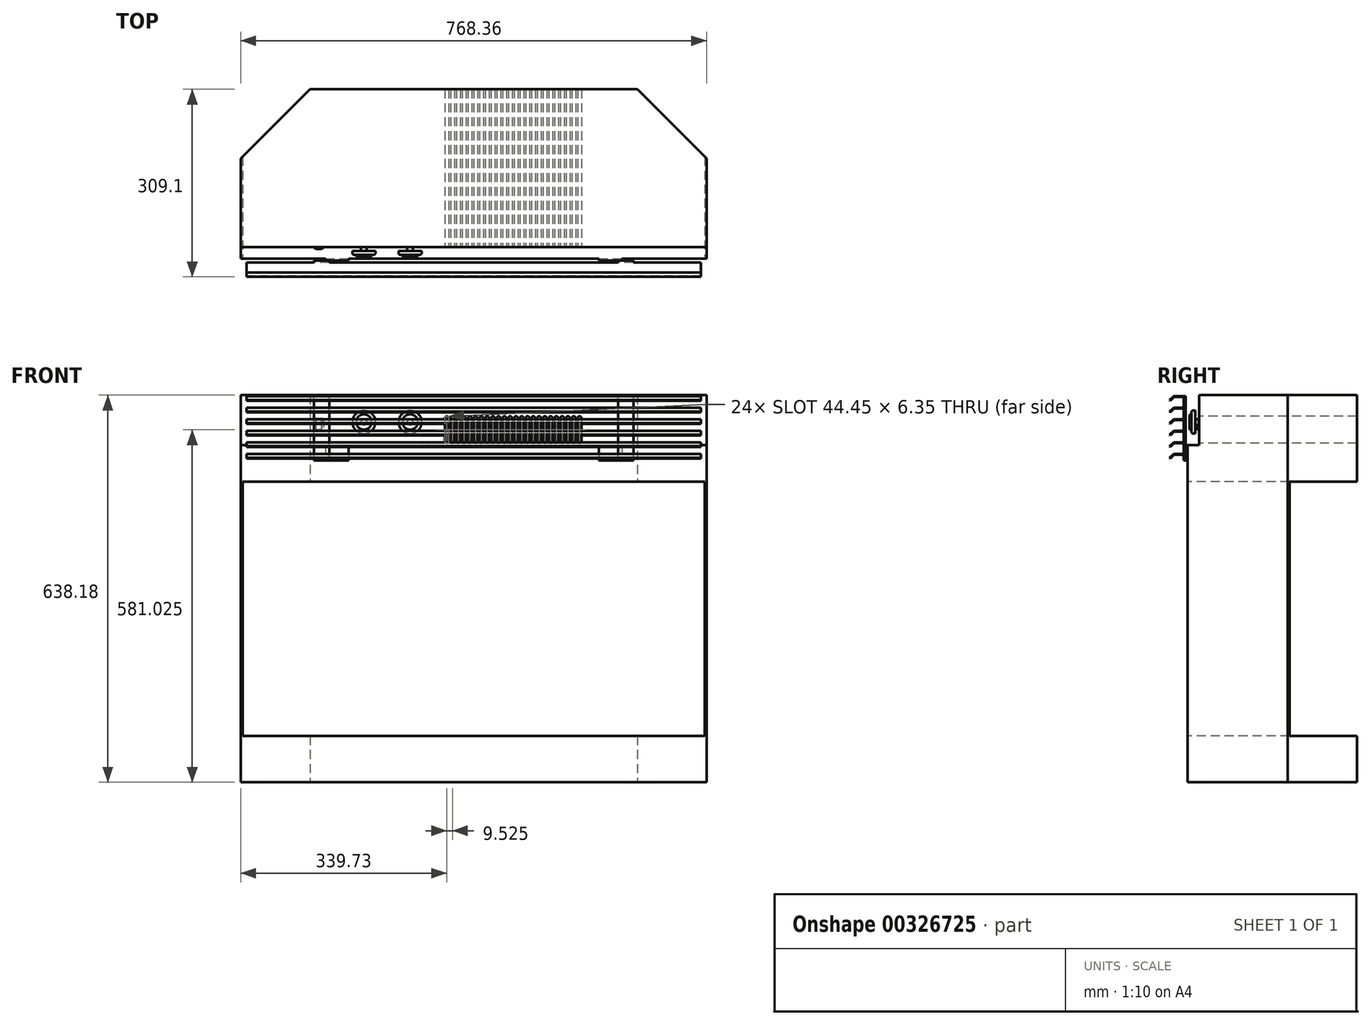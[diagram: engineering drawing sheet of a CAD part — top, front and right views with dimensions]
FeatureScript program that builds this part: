
annotation { "Feature Type Name" : "Feature", "Feature Type Description" : "" }
export const myFeature = defineFeature(function(context is Context, id is Id, definition is map)
    precondition{}
    {
        {
            var Q0;
            Q0=qCreatedBy(makeId("Top.planeOp"),FACE);
            var sketch = newSketch(context, id + "F0", { "sketchPlane" : qUnion([Q0])});
            skLineSegment(sketch, "E0.bottom", {"start": v(-269.88, 260.35) * mm, "end": v(269.88, 260.35) * mm});
            skLineSegment(sketch, "E0.top", {"start": v(-384.18, 0) * mm, "end": v(384.18, 0) * mm});
            skLineSegment(sketch, "E0.left", {"start": v(-384.18, 146.05) * mm, "end": v(-384.18, 0) * mm});
            skLineSegment(sketch, "E0.right", {"start": v(384.18, 146.05) * mm, "end": v(384.18, 0) * mm});
            skLineSegment(sketch, "E1", {"start": v(-384.18, 146.05) * mm, "end": v(-269.88, 260.35) * mm});
            skLineSegment(sketch, "E2", {"start": v(269.88, 260.35) * mm, "end": v(384.18, 146.05) * mm});
            skSolve(sketch);
        }
        {
            var Q0;
            Q0=makeQuery(id+"F0.imprint","IMPRINT",FACE,{"disambiguationData":[TD([[makeQuery(id+"F0.imprint","IMPRINT",EDGE,{"derivedFrom":sQuery(id+"F0.wireOp",EDGE,"E0.bottom")}),-1.0]])]});
            extrude(context, id + "F1", {"entities" : qUnion([Q0]), "depth" : 638.17 * mm});
        }
        {
            var Q0;
            Q0=makeQuery(id+"F1.opExtrude","SWEPT_FACE",FACE,{"disambiguationData":[OSD([sQuery(id+"F0.wireOp",EDGE,"E0.top")])]});
            var sketch = newSketch(context, id + "F2", { "sketchPlane" : qUnion([Q0])});
            skLineSegment(sketch, "E3.bottom", {"start": v(-384.18, 0) * mm, "end": v(384.18, 0) * mm});
            skLineSegment(sketch, "E3.top", {"start": v(-384.18, 555.62) * mm, "end": v(384.18, 555.62) * mm});
            skLineSegment(sketch, "E3.left", {"start": v(-384.18, 0) * mm, "end": v(-384.18, 555.62) * mm});
            skLineSegment(sketch, "E3.right", {"start": v(384.18, 0) * mm, "end": v(384.18, 555.62) * mm});
            skSolve(sketch);
        }
        {
            var Q0;
            Q0 = qSketchRegion(id + "F2", true);
            extrude(context, id + "F3", {"entities" : qUnion([Q0]), "operationType" : NewBodyOperationType.ADD, "depth" : 19.05 * mm});
        }
        {
            var Q0;
            Q0=makeQuery(id+"F3.opExtrude","CAP_FACE",FACE,{"disambiguationData":[OSD([sQuery(id+"F2.wireOp",EDGE,"E3.bottom"),sQuery(id+"F2.wireOp",EDGE,"E3.top"),sQuery(id+"F2.wireOp",EDGE,"E3.left"),sQuery(id+"F2.wireOp",EDGE,"E3.right")])],"isStart":false});
            var sketch = newSketch(context, id + "F4", { "sketchPlane" : qUnion([Q0])});
            skLineSegment(sketch, "E4.bottom", {"start": v(-381, 76.2) * mm, "end": v(381, 76.2) * mm});
            skLineSegment(sketch, "E4.top", {"start": v(-381, 495.3) * mm, "end": v(381, 495.3) * mm});
            skLineSegment(sketch, "E4.left", {"start": v(-381, 76.2) * mm, "end": v(-381, 495.3) * mm});
            skLineSegment(sketch, "E4.right", {"start": v(381, 76.2) * mm, "end": v(381, 495.3) * mm});
            skSolve(sketch);
        }
        {
            var Q0;
            Q0 = qSketchRegion(id + "F4", true);
            extrude(context, id + "F5", {"entities" : qUnion([Q0]), "operationType" : NewBodyOperationType.REMOVE, "endBound" : BoundingType.UP_TO_NEXT, "oppositeDirection" : true, "depth" : 6.35 * mm});
        }
        {
            var Q0;
            Q0=makeQuery(id+"F1.opExtrude","SWEPT_FACE",FACE,{"disambiguationData":[OSD([sQuery(id+"F0.wireOp",EDGE,"E0.top")])]});
            var sketch = newSketch(context, id + "F6", { "sketchPlane" : qUnion([Q0])});
            skCircle(sketch, "E5", {"center": v(-180.98, 593.73) * mm, "radius": 4.76 * mm});
            skCircle(sketch, "E6", {"center": v(-104.78, 593.73) * mm, "radius": 4.76 * mm});
            skSolve(sketch);
        }
        {
            var Q0;
            Q0=makeQuery(id+"F6.imprint","IMPRINT",FACE,{"disambiguationData":[TD([[makeQuery(id+"F6.imprint","IMPRINT",EDGE,{"derivedFrom":sQuery(id+"F6.wireOp",EDGE,"E5")}),1.0]])]});
            var Q1;
            Q1=makeQuery(id+"F6.imprint","IMPRINT",FACE,{"disambiguationData":[TD([[makeQuery(id+"F6.imprint","IMPRINT",EDGE,{"derivedFrom":sQuery(id+"F6.wireOp",EDGE,"E6")}),1.0]])]});
            extrude(context, id + "F7", {"entities" : qUnion([Q0, Q1]), "operationType" : NewBodyOperationType.ADD, "depth" : 6.35 * mm});
        }
        {
            var Q0;
            Q0=makeQuery(id+"F7.opExtrude","CAP_FACE",FACE,{"disambiguationData":[OSD([sQuery(id+"F6.wireOp",EDGE,"E5")])],"isStart":false});
            var sketch = newSketch(context, id + "F8", { "sketchPlane" : qUnion([Q0])});
            skCircle(sketch, "E7", {"center": v(-180.98, 593.73) * mm, "radius": 19.05 * mm});
            skCircle(sketch, "E8", {"center": v(-104.78, 593.73) * mm, "radius": 19.05 * mm});
            skSolve(sketch);
        }
        {
            var Q0;
            Q0=makeQuery(id+"F8.imprint","IMPRINT",FACE,{"disambiguationData":[TD([[makeQuery(id+"F8.imprint","IMPRINT",EDGE,{"derivedFrom":sQuery(id+"F8.wireOp",EDGE,"E8")}),1.0]])]});
            var Q1;
            Q1=makeQuery(id+"F8.imprint","IMPRINT",FACE,{"disambiguationData":[TD([[makeQuery(id+"F8.imprint","IMPRINT",EDGE,{"derivedFrom":sQuery(id+"F8.wireOp",EDGE,"E7")}),1.0]])]});
            var Q2;
            Q2=makeQuery(id+"F8.imprint","IMPRINT",FACE,{"disambiguationData":[TD([[makeQuery(id+"F8.imprint","IMPRINT",EDGE,{"derivedFrom":makeQuery(id+"F7.opExtrude","CAP_EDGE",EDGE,{"disambiguationData":[OSD([sQuery(id+"F6.wireOp",EDGE,"E5")])],"isStart":false})}),1.0]])]});
            extrude(context, id + "F9", {"entities" : qUnion([Q0, Q1, Q2]), "operationType" : NewBodyOperationType.ADD, "depth" : 6.35 * mm});
        }
        {
            var Q0;
            Q0=makeQuery(id+"F9.opExtrude","CAP_EDGE",EDGE,{"disambiguationData":[OSD([sQuery(id+"F8.wireOp",EDGE,"E8")])],"isStart":false});
            var Q1;
            Q1=makeQuery(id+"F9.opExtrude","CAP_EDGE",EDGE,{"disambiguationData":[OSD([sQuery(id+"F8.wireOp",EDGE,"E7")])],"isStart":false});
            fillet(context, id + "F10", {"entities" : qUnion([Q0, Q1]), "radius" : 3.17 * mm, "tangentPropagation" : true, "allowEdgeOverflow" : false});
        }
        {
            var Q0;
            Q0=makeQuery(id+"F9.opExtrude","CAP_FACE",FACE,{"disambiguationData":[OSD([sQuery(id+"F8.wireOp",EDGE,"E7")])],"isStart":false});
            var sketch = newSketch(context, id + "F11", { "sketchPlane" : qUnion([Q0])});
            skCircle(sketch, "E9", {"center": v(-180.98, 593.73) * mm, "radius": 12.7 * mm});
            skCircle(sketch, "E10", {"center": v(-104.78, 593.73) * mm, "radius": 12.7 * mm});
            skSolve(sketch);
        }
        {
            var Q0;
            Q0=makeQuery(id+"F11.imprint","IMPRINT",FACE,{"disambiguationData":[TD([[makeQuery(id+"F11.imprint","IMPRINT",EDGE,{"derivedFrom":sQuery(id+"F11.wireOp",EDGE,"E9")}),1.0]])]});
            var Q1;
            Q1=makeQuery(id+"F11.imprint","IMPRINT",FACE,{"disambiguationData":[TD([[makeQuery(id+"F11.imprint","IMPRINT",EDGE,{"derivedFrom":sQuery(id+"F11.wireOp",EDGE,"E10")}),1.0]])]});
            extrude(context, id + "F12", {"entities" : qUnion([Q0, Q1]), "operationType" : NewBodyOperationType.ADD, "depth" : 3.17 * mm});
        }
        {
            var Q0;
            Q0=makeQuery(id+"F12.opExtrude","CAP_EDGE",EDGE,{"disambiguationData":[OSD([sQuery(id+"F11.wireOp",EDGE,"E9")])],"isStart":false});
            var Q1;
            Q1=makeQuery(id+"F12.opExtrude","CAP_EDGE",EDGE,{"disambiguationData":[OSD([sQuery(id+"F11.wireOp",EDGE,"E10")])],"isStart":false});
            fillet(context, id + "F13", {"entities" : qUnion([Q0, Q1]), "radius" : 2.3 * mm, "tangentPropagation" : true, "allowEdgeOverflow" : false});
        }
        {
            var Q0;
            Q0=makeQuery(id+"F1.opExtrude","SWEPT_FACE",FACE,{"disambiguationData":[OSD([sQuery(id+"F0.wireOp",EDGE,"E0.top")])]});
            var sketch = newSketch(context, id + "F14", { "sketchPlane" : qUnion([Q0])});
            skLineSegment(sketch, "E11", {"start": v(-44.45, 600.08) * mm, "end": v(-44.45, 561.98) * mm, "construction": true});
            skArc(sketch, "E12.0.startCap", {"start": v(-47.62, 600.08) * mm, "mid": v(-44.45, 603.25) * mm, "end": v(-41.27, 600.08) * mm});
            skArc(sketch, "E12.0.endCap", {"start": v(-41.27, 561.98) * mm, "mid": v(-44.45, 558.8) * mm, "end": v(-47.62, 561.98) * mm});
            skLineSegment(sketch, "E12.0.left", {"start": v(-41.27, 600.08) * mm, "end": v(-41.27, 561.98) * mm});
            skLineSegment(sketch, "E12.0.right", {"start": v(-47.62, 600.08) * mm, "end": v(-47.62, 561.98) * mm});
            skLineSegment(sketch, "E13.1.0.0", {"start": v(-31.75, 600.08) * mm, "end": v(-31.75, 561.98) * mm});
            skArc(sketch, "E13.1.0.1", {"start": v(-38.1, 600.08) * mm, "mid": v(-34.92, 603.25) * mm, "end": v(-31.75, 600.08) * mm});
            skLineSegment(sketch, "E13.1.0.2", {"start": v(-38.1, 600.08) * mm, "end": v(-38.1, 561.98) * mm});
            skArc(sketch, "E13.1.0.3", {"start": v(-31.75, 561.98) * mm, "mid": v(-34.92, 558.8) * mm, "end": v(-38.1, 561.98) * mm});
            skLineSegment(sketch, "E13.2.0.0", {"start": v(-22.22, 600.08) * mm, "end": v(-22.22, 561.98) * mm});
            skArc(sketch, "E13.2.0.1", {"start": v(-28.57, 600.08) * mm, "mid": v(-25.4, 603.25) * mm, "end": v(-22.22, 600.08) * mm});
            skLineSegment(sketch, "E13.2.0.2", {"start": v(-28.57, 600.08) * mm, "end": v(-28.57, 561.98) * mm});
            skArc(sketch, "E13.2.0.3", {"start": v(-22.22, 561.98) * mm, "mid": v(-25.4, 558.8) * mm, "end": v(-28.57, 561.98) * mm});
            skLineSegment(sketch, "E13.3.0.0", {"start": v(-12.7, 600.08) * mm, "end": v(-12.7, 561.98) * mm});
            skArc(sketch, "E13.3.0.1", {"start": v(-19.05, 600.08) * mm, "mid": v(-15.87, 603.25) * mm, "end": v(-12.7, 600.08) * mm});
            skLineSegment(sketch, "E13.3.0.2", {"start": v(-19.05, 600.08) * mm, "end": v(-19.05, 561.98) * mm});
            skArc(sketch, "E13.3.0.3", {"start": v(-12.7, 561.98) * mm, "mid": v(-15.87, 558.8) * mm, "end": v(-19.05, 561.98) * mm});
            skLineSegment(sketch, "E13.4.0.0", {"start": v(-3.17, 600.08) * mm, "end": v(-3.17, 561.98) * mm});
            skArc(sketch, "E13.4.0.1", {"start": v(-9.52, 600.08) * mm, "mid": v(-6.35, 603.25) * mm, "end": v(-3.17, 600.08) * mm});
            skLineSegment(sketch, "E13.4.0.2", {"start": v(-9.52, 600.08) * mm, "end": v(-9.52, 561.98) * mm});
            skArc(sketch, "E13.4.0.3", {"start": v(-3.17, 561.98) * mm, "mid": v(-6.35, 558.8) * mm, "end": v(-9.52, 561.98) * mm});
            skLineSegment(sketch, "E13.5.0.0", {"start": v(6.35, 600.08) * mm, "end": v(6.35, 561.98) * mm});
            skArc(sketch, "E13.5.0.1", {"start": v(0, 600.08) * mm, "mid": v(3.18, 603.25) * mm, "end": v(6.35, 600.08) * mm});
            skLineSegment(sketch, "E13.5.0.2", {"start": v(0, 600.08) * mm, "end": v(0, 561.98) * mm});
            skArc(sketch, "E13.5.0.3", {"start": v(6.35, 561.98) * mm, "mid": v(3.18, 558.8) * mm, "end": v(0, 561.98) * mm});
            skLineSegment(sketch, "E13.6.0.0", {"start": v(15.88, 600.08) * mm, "end": v(15.88, 561.98) * mm});
            skArc(sketch, "E13.6.0.1", {"start": v(9.53, 600.08) * mm, "mid": v(12.7, 603.25) * mm, "end": v(15.88, 600.08) * mm});
            skLineSegment(sketch, "E13.6.0.2", {"start": v(9.53, 600.08) * mm, "end": v(9.53, 561.98) * mm});
            skArc(sketch, "E13.6.0.3", {"start": v(15.88, 561.98) * mm, "mid": v(12.7, 558.8) * mm, "end": v(9.53, 561.98) * mm});
            skLineSegment(sketch, "E13.7.0.0", {"start": v(25.4, 600.08) * mm, "end": v(25.4, 561.98) * mm});
            skArc(sketch, "E13.7.0.1", {"start": v(19.05, 600.08) * mm, "mid": v(22.23, 603.25) * mm, "end": v(25.4, 600.08) * mm});
            skLineSegment(sketch, "E13.7.0.2", {"start": v(19.05, 600.08) * mm, "end": v(19.05, 561.98) * mm});
            skArc(sketch, "E13.7.0.3", {"start": v(25.4, 561.98) * mm, "mid": v(22.23, 558.8) * mm, "end": v(19.05, 561.98) * mm});
            skLineSegment(sketch, "E13.8.0.0", {"start": v(34.93, 600.08) * mm, "end": v(34.93, 561.98) * mm});
            skArc(sketch, "E13.8.0.1", {"start": v(28.58, 600.08) * mm, "mid": v(31.75, 603.25) * mm, "end": v(34.93, 600.08) * mm});
            skLineSegment(sketch, "E13.8.0.2", {"start": v(28.58, 600.08) * mm, "end": v(28.58, 561.98) * mm});
            skArc(sketch, "E13.8.0.3", {"start": v(34.93, 561.98) * mm, "mid": v(31.75, 558.8) * mm, "end": v(28.58, 561.98) * mm});
            skLineSegment(sketch, "E13.9.0.0", {"start": v(44.45, 600.08) * mm, "end": v(44.45, 561.98) * mm});
            skArc(sketch, "E13.9.0.1", {"start": v(38.1, 600.08) * mm, "mid": v(41.28, 603.25) * mm, "end": v(44.45, 600.08) * mm});
            skLineSegment(sketch, "E13.9.0.2", {"start": v(38.1, 600.08) * mm, "end": v(38.1, 561.98) * mm});
            skArc(sketch, "E13.9.0.3", {"start": v(44.45, 561.98) * mm, "mid": v(41.28, 558.8) * mm, "end": v(38.1, 561.98) * mm});
            skLineSegment(sketch, "E13.10.0.0", {"start": v(53.98, 600.08) * mm, "end": v(53.98, 561.98) * mm});
            skArc(sketch, "E13.10.0.1", {"start": v(47.63, 600.08) * mm, "mid": v(50.8, 603.25) * mm, "end": v(53.98, 600.08) * mm});
            skLineSegment(sketch, "E13.10.0.2", {"start": v(47.63, 600.08) * mm, "end": v(47.63, 561.98) * mm});
            skArc(sketch, "E13.10.0.3", {"start": v(53.98, 561.98) * mm, "mid": v(50.8, 558.8) * mm, "end": v(47.63, 561.98) * mm});
            skLineSegment(sketch, "E13.11.0.0", {"start": v(63.5, 600.08) * mm, "end": v(63.5, 561.98) * mm});
            skArc(sketch, "E13.11.0.1", {"start": v(57.15, 600.08) * mm, "mid": v(60.33, 603.25) * mm, "end": v(63.5, 600.08) * mm});
            skLineSegment(sketch, "E13.11.0.2", {"start": v(57.15, 600.08) * mm, "end": v(57.15, 561.98) * mm});
            skArc(sketch, "E13.11.0.3", {"start": v(63.5, 561.98) * mm, "mid": v(60.33, 558.8) * mm, "end": v(57.15, 561.98) * mm});
            skLineSegment(sketch, "E13.12.0.0", {"start": v(73.03, 600.08) * mm, "end": v(73.03, 561.98) * mm});
            skArc(sketch, "E13.12.0.1", {"start": v(66.68, 600.08) * mm, "mid": v(69.85, 603.25) * mm, "end": v(73.03, 600.08) * mm});
            skLineSegment(sketch, "E13.12.0.2", {"start": v(66.68, 600.08) * mm, "end": v(66.68, 561.98) * mm});
            skArc(sketch, "E13.12.0.3", {"start": v(73.03, 561.98) * mm, "mid": v(69.85, 558.8) * mm, "end": v(66.68, 561.98) * mm});
            skLineSegment(sketch, "E13.13.0.0", {"start": v(82.55, 600.08) * mm, "end": v(82.55, 561.98) * mm});
            skArc(sketch, "E13.13.0.1", {"start": v(76.2, 600.08) * mm, "mid": v(79.38, 603.25) * mm, "end": v(82.55, 600.08) * mm});
            skLineSegment(sketch, "E13.13.0.2", {"start": v(76.2, 600.08) * mm, "end": v(76.2, 561.98) * mm});
            skArc(sketch, "E13.13.0.3", {"start": v(82.55, 561.98) * mm, "mid": v(79.38, 558.8) * mm, "end": v(76.2, 561.98) * mm});
            skLineSegment(sketch, "E13.14.0.0", {"start": v(92.08, 600.08) * mm, "end": v(92.08, 561.98) * mm});
            skArc(sketch, "E13.14.0.1", {"start": v(85.73, 600.08) * mm, "mid": v(88.9, 603.25) * mm, "end": v(92.08, 600.08) * mm});
            skLineSegment(sketch, "E13.14.0.2", {"start": v(85.73, 600.08) * mm, "end": v(85.73, 561.98) * mm});
            skArc(sketch, "E13.14.0.3", {"start": v(92.08, 561.98) * mm, "mid": v(88.9, 558.8) * mm, "end": v(85.73, 561.98) * mm});
            skLineSegment(sketch, "E13.15.0.0", {"start": v(101.6, 600.08) * mm, "end": v(101.6, 561.98) * mm});
            skArc(sketch, "E13.15.0.1", {"start": v(95.25, 600.08) * mm, "mid": v(98.43, 603.25) * mm, "end": v(101.6, 600.08) * mm});
            skLineSegment(sketch, "E13.15.0.2", {"start": v(95.25, 600.08) * mm, "end": v(95.25, 561.98) * mm});
            skArc(sketch, "E13.15.0.3", {"start": v(101.6, 561.98) * mm, "mid": v(98.43, 558.8) * mm, "end": v(95.25, 561.98) * mm});
            skLineSegment(sketch, "E13.16.0.0", {"start": v(111.13, 600.08) * mm, "end": v(111.13, 561.98) * mm});
            skArc(sketch, "E13.16.0.1", {"start": v(104.78, 600.08) * mm, "mid": v(107.95, 603.25) * mm, "end": v(111.13, 600.08) * mm});
            skLineSegment(sketch, "E13.16.0.2", {"start": v(104.78, 600.08) * mm, "end": v(104.78, 561.98) * mm});
            skArc(sketch, "E13.16.0.3", {"start": v(111.13, 561.98) * mm, "mid": v(107.95, 558.8) * mm, "end": v(104.78, 561.98) * mm});
            skLineSegment(sketch, "E13.17.0.0", {"start": v(120.65, 600.08) * mm, "end": v(120.65, 561.98) * mm});
            skArc(sketch, "E13.17.0.1", {"start": v(114.3, 600.08) * mm, "mid": v(117.48, 603.25) * mm, "end": v(120.65, 600.08) * mm});
            skLineSegment(sketch, "E13.17.0.2", {"start": v(114.3, 600.08) * mm, "end": v(114.3, 561.98) * mm});
            skArc(sketch, "E13.17.0.3", {"start": v(120.65, 561.98) * mm, "mid": v(117.48, 558.8) * mm, "end": v(114.3, 561.98) * mm});
            skLineSegment(sketch, "E13.18.0.0", {"start": v(130.18, 600.08) * mm, "end": v(130.18, 561.98) * mm});
            skArc(sketch, "E13.18.0.1", {"start": v(123.83, 600.08) * mm, "mid": v(127, 603.25) * mm, "end": v(130.18, 600.08) * mm});
            skLineSegment(sketch, "E13.18.0.2", {"start": v(123.83, 600.08) * mm, "end": v(123.83, 561.98) * mm});
            skArc(sketch, "E13.18.0.3", {"start": v(130.18, 561.98) * mm, "mid": v(127, 558.8) * mm, "end": v(123.83, 561.98) * mm});
            skLineSegment(sketch, "E13.19.0.0", {"start": v(139.7, 600.08) * mm, "end": v(139.7, 561.98) * mm});
            skArc(sketch, "E13.19.0.1", {"start": v(133.35, 600.08) * mm, "mid": v(136.53, 603.25) * mm, "end": v(139.7, 600.08) * mm});
            skLineSegment(sketch, "E13.19.0.2", {"start": v(133.35, 600.08) * mm, "end": v(133.35, 561.98) * mm});
            skArc(sketch, "E13.19.0.3", {"start": v(139.7, 561.98) * mm, "mid": v(136.53, 558.8) * mm, "end": v(133.35, 561.98) * mm});
            skLineSegment(sketch, "E13.20.0.0", {"start": v(149.23, 600.08) * mm, "end": v(149.23, 561.98) * mm});
            skArc(sketch, "E13.20.0.1", {"start": v(142.88, 600.08) * mm, "mid": v(146.05, 603.25) * mm, "end": v(149.23, 600.08) * mm});
            skLineSegment(sketch, "E13.20.0.2", {"start": v(142.88, 600.08) * mm, "end": v(142.88, 561.98) * mm});
            skArc(sketch, "E13.20.0.3", {"start": v(149.23, 561.98) * mm, "mid": v(146.05, 558.8) * mm, "end": v(142.88, 561.98) * mm});
            skLineSegment(sketch, "E13.21.0.0", {"start": v(158.75, 600.08) * mm, "end": v(158.75, 561.98) * mm});
            skArc(sketch, "E13.21.0.1", {"start": v(152.4, 600.08) * mm, "mid": v(155.58, 603.25) * mm, "end": v(158.75, 600.08) * mm});
            skLineSegment(sketch, "E13.21.0.2", {"start": v(152.4, 600.08) * mm, "end": v(152.4, 561.98) * mm});
            skArc(sketch, "E13.21.0.3", {"start": v(158.75, 561.98) * mm, "mid": v(155.58, 558.8) * mm, "end": v(152.4, 561.98) * mm});
            skLineSegment(sketch, "E13.22.0.0", {"start": v(168.28, 600.08) * mm, "end": v(168.28, 561.98) * mm});
            skArc(sketch, "E13.22.0.1", {"start": v(161.93, 600.08) * mm, "mid": v(165.1, 603.25) * mm, "end": v(168.28, 600.08) * mm});
            skLineSegment(sketch, "E13.22.0.2", {"start": v(161.93, 600.08) * mm, "end": v(161.93, 561.98) * mm});
            skArc(sketch, "E13.22.0.3", {"start": v(168.28, 561.98) * mm, "mid": v(165.1, 558.8) * mm, "end": v(161.93, 561.98) * mm});
            skLineSegment(sketch, "E13.23.0.0", {"start": v(177.8, 600.08) * mm, "end": v(177.8, 561.98) * mm});
            skArc(sketch, "E13.23.0.1", {"start": v(171.45, 600.08) * mm, "mid": v(174.63, 603.25) * mm, "end": v(177.8, 600.08) * mm});
            skLineSegment(sketch, "E13.23.0.2", {"start": v(171.45, 600.08) * mm, "end": v(171.45, 561.98) * mm});
            skArc(sketch, "E13.23.0.3", {"start": v(177.8, 561.98) * mm, "mid": v(174.63, 558.8) * mm, "end": v(171.45, 561.98) * mm});
            skLineSegment(sketch, "E13.direction1", {"start": v(-47.62, 561.98) * mm, "end": v(-38.1, 561.98) * mm, "construction": true});
            skSolve(sketch);
        }
        {
            var Q0;
            Q0 = qSketchRegion(id + "F14", true);
            extrude(context, id + "F15", {"entities" : qUnion([Q0]), "operationType" : NewBodyOperationType.REMOVE, "endBound" : BoundingType.UP_TO_NEXT, "oppositeDirection" : true, "depth" : 25.4 * mm});
        }
        {
            var Q0;
            Q0=makeQuery(id+"F1.opExtrude","SWEPT_FACE",FACE,{"disambiguationData":[OSD([sQuery(id+"F0.wireOp",EDGE,"E0.top")])]});
            var sketch = newSketch(context, id + "F16", { "sketchPlane" : qUnion([Q0])});
            skLineSegment(sketch, "E14.bottom", {"start": v(-263.53, 600.08) * mm, "end": v(-247.65, 600.08) * mm});
            skLineSegment(sketch, "E14.top", {"start": v(-263.53, 580.23) * mm, "end": v(-247.65, 580.23) * mm});
            skLineSegment(sketch, "E14.left", {"start": v(-263.53, 600.08) * mm, "end": v(-263.53, 580.23) * mm});
            skLineSegment(sketch, "E14.right", {"start": v(-247.65, 600.08) * mm, "end": v(-247.65, 580.23) * mm});
            skSolve(sketch);
        }
        {
            var Q0;
            Q0=makeQuery(id+"F16.imprint","IMPRINT",FACE,{"disambiguationData":[TD([[makeQuery(id+"F16.imprint","IMPRINT",EDGE,{"derivedFrom":sQuery(id+"F16.wireOp",EDGE,"E14.bottom")}),-1.0]])]});
            extrude(context, id + "F17", {"entities" : qUnion([Q0]), "operationType" : NewBodyOperationType.ADD, "depth" : 1.59 * mm});
        }
        {
            var Q0;
            Q0=makeQuery(id+"F17.opExtrude","SWEPT_FACE",FACE,{"disambiguationData":[OSD([sQuery(id+"F16.wireOp",EDGE,"E14.left")])]});
            cPlane(context, id + "F18", {"entities" : qUnion([Q0]), "cplaneType" : CPlaneType.OFFSET, "offset" : 7.94 * mm, "oppositeDirection" : true, "width" : 152.4 * mm, "height" : 152.4 * mm});
        }
        {
            var Q0;
            Q0=qCreatedBy(id+"F18.planeOp",FACE);
            var sketch = newSketch(context, id + "F19", { "sketchPlane" : qUnion([Q0])});
            skLineSegment(sketch, "E15", {"start": v(1.59, 597.7) * mm, "end": v(2.35, 597.7) * mm});
            skLineSegment(sketch, "E16", {"start": v(2.35, 597.7) * mm, "end": v(2.35, 589.76) * mm});
            skLineSegment(sketch, "E17", {"start": v(2.35, 589.76) * mm, "end": v(3.1, 581.9) * mm});
            skLineSegment(sketch, "E18", {"start": v(3.1, 581.9) * mm, "end": v(2.35, 581.82) * mm});
            skLineSegment(sketch, "E19", {"start": v(2.35, 581.82) * mm, "end": v(1.59, 581.82) * mm});
            skLineSegment(sketch, "E20", {"start": v(1.59, 581.82) * mm, "end": v(1.59, 597.7) * mm});
            skSolve(sketch);
        }
        {
            var Q0;
            Q0=makeQuery(id+"F19.imprint","IMPRINT",FACE,{"disambiguationData":[TD([[makeQuery(id+"F19.imprint","IMPRINT",EDGE,{"derivedFrom":sQuery(id+"F19.wireOp",EDGE,"E15")}),-1.0]])]});
            extrude(context, id + "F20", {"entities" : qUnion([Q0]), "operationType" : NewBodyOperationType.ADD, "endBound" : BoundingType.SYMMETRIC, "depth" : 9.52 * mm});
        }
        {
            var Q0;
            Q0=makeQuery(id+"F3.opExtrude","CAP_FACE",FACE,{"disambiguationData":[OSD([sQuery(id+"F2.wireOp",EDGE,"E3.bottom"),sQuery(id+"F2.wireOp",EDGE,"E3.top"),sQuery(id+"F2.wireOp",EDGE,"E3.left"),sQuery(id+"F2.wireOp",EDGE,"E3.right")])],"isStart":false});
            var sketch = newSketch(context, id + "F21", { "sketchPlane" : qUnion([Q0])});
            skLineSegment(sketch, "E21.bottom", {"start": v(-244.48, 555.62) * mm, "end": v(-206.38, 555.62) * mm});
            skLineSegment(sketch, "E21.top", {"start": v(-244.48, 530.23) * mm, "end": v(-206.38, 530.23) * mm});
            skLineSegment(sketch, "E21.left", {"start": v(-244.48, 555.62) * mm, "end": v(-244.48, 530.23) * mm});
            skLineSegment(sketch, "E21.right", {"start": v(-206.38, 555.62) * mm, "end": v(-206.38, 530.23) * mm});
            skLineSegment(sketch, "E22.bottom", {"start": v(206.38, 555.62) * mm, "end": v(244.48, 555.62) * mm});
            skLineSegment(sketch, "E22.top", {"start": v(206.38, 530.23) * mm, "end": v(244.48, 530.23) * mm});
            skLineSegment(sketch, "E22.left", {"start": v(206.38, 555.62) * mm, "end": v(206.38, 530.23) * mm});
            skLineSegment(sketch, "E22.right", {"start": v(244.48, 555.62) * mm, "end": v(244.48, 530.23) * mm});
            skSolve(sketch);
        }
        {
            var Q0;
            Q0=makeQuery(id+"F21.imprint","IMPRINT",FACE,{"disambiguationData":[TD([[makeQuery(id+"F21.imprint","IMPRINT",EDGE,{"derivedFrom":sQuery(id+"F21.wireOp",EDGE,"E21.bottom")}),-1.0]])]});
            var Q1;
            Q1=makeQuery(id+"F21.imprint","IMPRINT",FACE,{"disambiguationData":[TD([[makeQuery(id+"F21.imprint","IMPRINT",EDGE,{"derivedFrom":sQuery(id+"F21.wireOp",EDGE,"E22.bottom")}),-1.0]])]});
            extrude(context, id + "F22", {"entities" : qUnion([Q0, Q1]), "operationType" : NewBodyOperationType.ADD, "depth" : 3.17 * mm});
        }
        {
            var Q0;
            Q0=makeQuery(id+"F22.opExtrude","CAP_FACE",FACE,{"disambiguationData":[OSD([sQuery(id+"F21.wireOp",EDGE,"E21.bottom"),sQuery(id+"F21.wireOp",EDGE,"E21.top"),sQuery(id+"F21.wireOp",EDGE,"E21.left"),sQuery(id+"F21.wireOp",EDGE,"E21.right")])],"isStart":false});
            var sketch = newSketch(context, id + "F23", { "sketchPlane" : qUnion([Q0])});
            skLineSegment(sketch, "E23.bottom", {"start": v(-238.13, 530.23) * mm, "end": v(-263.53, 530.23) * mm});
            skLineSegment(sketch, "E23.top", {"start": v(-238.13, 636.59) * mm, "end": v(-263.53, 636.59) * mm});
            skLineSegment(sketch, "E23.left", {"start": v(-238.13, 530.23) * mm, "end": v(-238.13, 636.59) * mm});
            skLineSegment(sketch, "E23.right", {"start": v(-263.53, 530.23) * mm, "end": v(-263.53, 636.59) * mm});
            skLineSegment(sketch, "E24.bottom", {"start": v(238.13, 530.23) * mm, "end": v(263.53, 530.23) * mm});
            skLineSegment(sketch, "E24.top", {"start": v(238.13, 636.59) * mm, "end": v(263.53, 636.59) * mm});
            skLineSegment(sketch, "E24.left", {"start": v(238.13, 530.23) * mm, "end": v(238.13, 636.59) * mm});
            skLineSegment(sketch, "E24.right", {"start": v(263.53, 530.23) * mm, "end": v(263.53, 636.59) * mm});
            skSolve(sketch);
        }
        {
            var Q0;
            Q0 = qSketchRegion(id + "F23", true);
            extrude(context, id + "F24", {"entities" : qUnion([Q0]), "operationType" : NewBodyOperationType.ADD, "depth" : 3.17 * mm});
        }
        {
            var Q0;
            Q0=qCreatedBy(makeId("Right.planeOp"),FACE);
            var sketch = newSketch(context, id + "F25", { "sketchPlane" : qUnion([Q0])});
            skLineSegment(sketch, "E25", {"start": v(-25.4, 636.59) * mm, "end": v(-41.93, 636.59) * mm});
            skLineSegment(sketch, "E26", {"start": v(-41.93, 636.59) * mm, "end": v(-48.75, 629.77) * mm});
            skLineSegment(sketch, "E27", {"start": v(-48.75, 629.77) * mm, "end": v(-47.62, 628.65) * mm});
            skLineSegment(sketch, "E28", {"start": v(-47.62, 628.65) * mm, "end": v(-41.27, 635) * mm});
            skLineSegment(sketch, "E29", {"start": v(-41.27, 635) * mm, "end": v(-25.4, 635) * mm});
            skLineSegment(sketch, "E30", {"start": v(-25.4, 635) * mm, "end": v(-25.4, 636.59) * mm});
            skLineSegment(sketch, "E31.0.1.0", {"start": v(-41.93, 617.54) * mm, "end": v(-48.75, 610.72) * mm});
            skLineSegment(sketch, "E31.0.1.1", {"start": v(-25.4, 617.54) * mm, "end": v(-41.93, 617.54) * mm});
            skLineSegment(sketch, "E31.0.1.2", {"start": v(-48.75, 610.72) * mm, "end": v(-47.62, 609.6) * mm});
            skLineSegment(sketch, "E31.0.1.3", {"start": v(-47.62, 609.6) * mm, "end": v(-41.27, 615.95) * mm});
            skLineSegment(sketch, "E31.0.1.4", {"start": v(-25.4, 615.95) * mm, "end": v(-25.4, 617.54) * mm});
            skLineSegment(sketch, "E31.0.1.5", {"start": v(-41.27, 615.95) * mm, "end": v(-25.4, 615.95) * mm});
            skLineSegment(sketch, "E31.0.2.0", {"start": v(-41.93, 598.49) * mm, "end": v(-48.75, 591.67) * mm});
            skLineSegment(sketch, "E31.0.2.1", {"start": v(-25.4, 598.49) * mm, "end": v(-41.93, 598.49) * mm});
            skLineSegment(sketch, "E31.0.2.2", {"start": v(-48.75, 591.67) * mm, "end": v(-47.62, 590.55) * mm});
            skLineSegment(sketch, "E31.0.2.3", {"start": v(-47.62, 590.55) * mm, "end": v(-41.27, 596.9) * mm});
            skLineSegment(sketch, "E31.0.2.4", {"start": v(-25.4, 596.9) * mm, "end": v(-25.4, 598.49) * mm});
            skLineSegment(sketch, "E31.0.2.5", {"start": v(-41.27, 596.9) * mm, "end": v(-25.4, 596.9) * mm});
            skLineSegment(sketch, "E31.0.3.0", {"start": v(-41.93, 579.44) * mm, "end": v(-48.75, 572.62) * mm});
            skLineSegment(sketch, "E31.0.3.1", {"start": v(-25.4, 579.44) * mm, "end": v(-41.93, 579.44) * mm});
            skLineSegment(sketch, "E31.0.3.2", {"start": v(-48.75, 572.62) * mm, "end": v(-47.62, 571.5) * mm});
            skLineSegment(sketch, "E31.0.3.3", {"start": v(-47.62, 571.5) * mm, "end": v(-41.27, 577.85) * mm});
            skLineSegment(sketch, "E31.0.3.4", {"start": v(-25.4, 577.85) * mm, "end": v(-25.4, 579.44) * mm});
            skLineSegment(sketch, "E31.0.3.5", {"start": v(-41.27, 577.85) * mm, "end": v(-25.4, 577.85) * mm});
            skLineSegment(sketch, "E31.0.4.0", {"start": v(-41.93, 560.39) * mm, "end": v(-48.75, 553.57) * mm});
            skLineSegment(sketch, "E31.0.4.1", {"start": v(-25.4, 560.39) * mm, "end": v(-41.93, 560.39) * mm});
            skLineSegment(sketch, "E31.0.4.2", {"start": v(-48.75, 553.57) * mm, "end": v(-47.62, 552.45) * mm});
            skLineSegment(sketch, "E31.0.4.3", {"start": v(-47.62, 552.45) * mm, "end": v(-41.27, 558.8) * mm});
            skLineSegment(sketch, "E31.0.4.4", {"start": v(-25.4, 558.8) * mm, "end": v(-25.4, 560.39) * mm});
            skLineSegment(sketch, "E31.0.4.5", {"start": v(-41.27, 558.8) * mm, "end": v(-25.4, 558.8) * mm});
            skLineSegment(sketch, "E31.0.5.0", {"start": v(-41.93, 541.34) * mm, "end": v(-48.75, 534.52) * mm});
            skLineSegment(sketch, "E31.0.5.1", {"start": v(-25.4, 541.34) * mm, "end": v(-41.93, 541.34) * mm});
            skLineSegment(sketch, "E31.0.5.2", {"start": v(-48.75, 534.52) * mm, "end": v(-47.62, 533.4) * mm});
            skLineSegment(sketch, "E31.0.5.3", {"start": v(-47.62, 533.4) * mm, "end": v(-41.27, 539.75) * mm});
            skLineSegment(sketch, "E31.0.5.4", {"start": v(-25.4, 539.75) * mm, "end": v(-25.4, 541.34) * mm});
            skLineSegment(sketch, "E31.0.5.5", {"start": v(-41.27, 539.75) * mm, "end": v(-25.4, 539.75) * mm});
            skLineSegment(sketch, "E31.direction1", {"start": v(-41.93, 636.59) * mm, "end": v(-16.53, 636.59) * mm, "construction": true});
            skLineSegment(sketch, "E31.direction2", {"start": v(-41.93, 636.59) * mm, "end": v(-41.93, 617.54) * mm, "construction": true});
            skSolve(sketch);
        }
        {
            var Q0;
            Q0 = qSketchRegion(id + "F25", true);
            extrude(context, id + "F26", {"entities" : qUnion([Q0]), "operationType" : NewBodyOperationType.ADD, "endBound" : BoundingType.SYMMETRIC, "depth" : 749.3 * mm});
        }
    });
